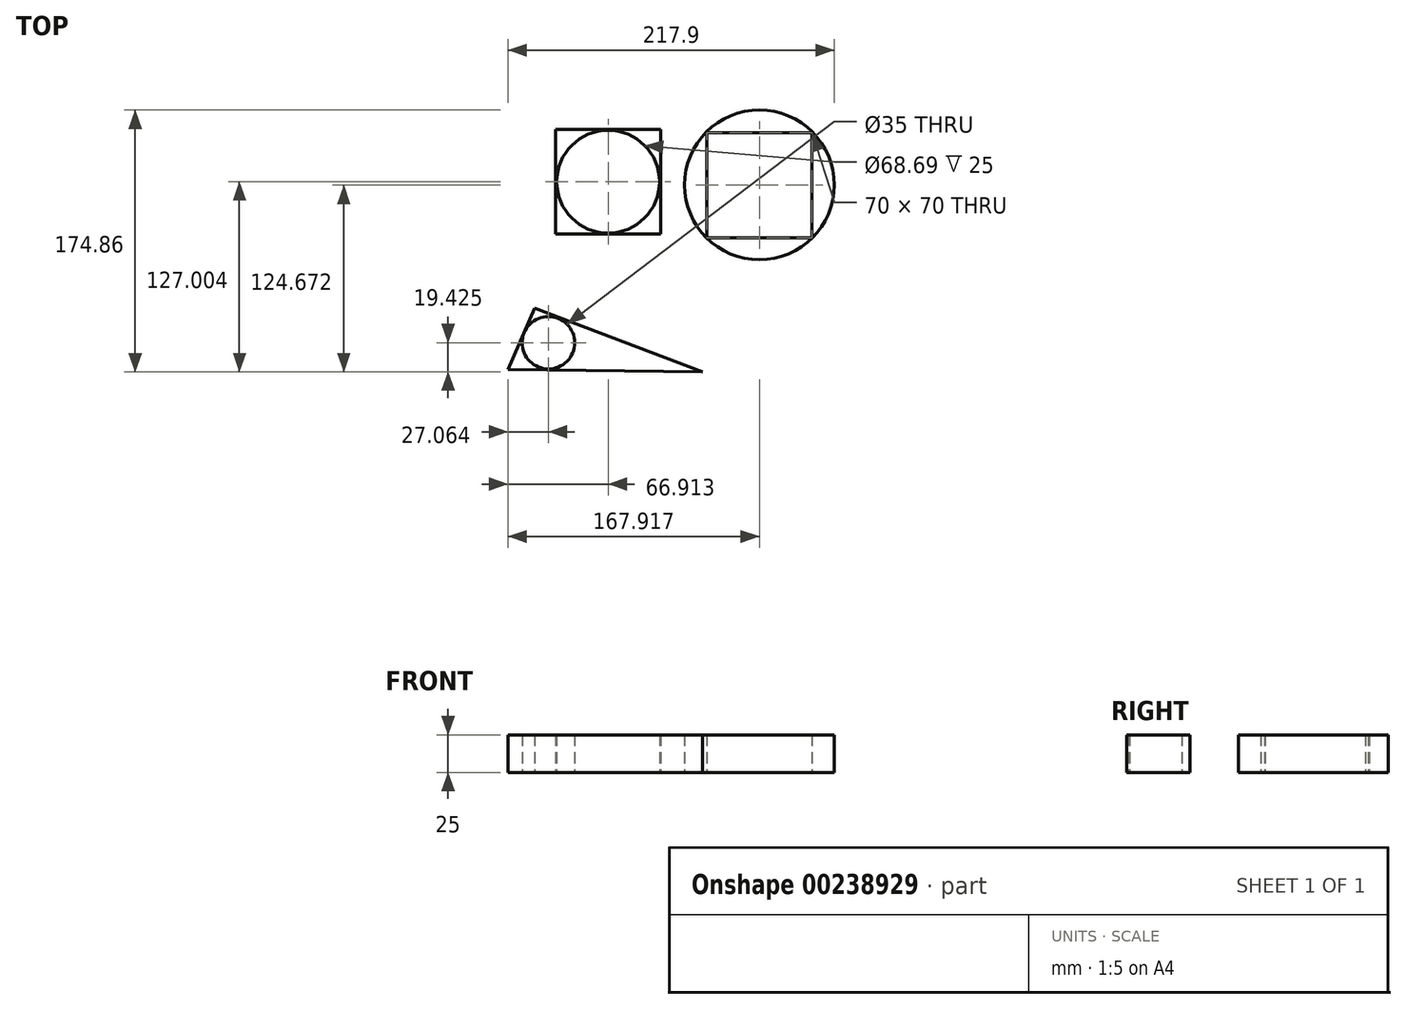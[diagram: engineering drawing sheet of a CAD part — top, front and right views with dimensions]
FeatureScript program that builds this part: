
annotation { "Feature Type Name" : "Feature", "Feature Type Description" : "" }
export const myFeature = defineFeature(function(context is Context, id is Id, definition is map)
    precondition{}
    {
        {
            var Q0;
            Q0=qCreatedBy(makeId("Top.planeOp"),FACE);
            var sketch = newSketch(context, id + "F0", { "sketchPlane" : qUnion([Q0])});
            skLineSegment(sketch, "E0", {"start": v(17.6, -74.14) * mm, "end": v(-94.65, -31.74) * mm});
            skLineSegment(sketch, "E1", {"start": v(17.6, -74.14) * mm, "end": v(-112.38, -72.57) * mm});
            skLineSegment(sketch, "E2", {"start": v(-94.65, -31.74) * mm, "end": v(-112.38, -72.57) * mm});
            skCircle(sketch, "E3", {"center": v(-85.32, -54.71) * mm, "radius": 17.5 * mm});
            skLineSegment(sketch, "E4", {"start": v(90.54, 85.53) * mm, "end": v(90.54, 15.53) * mm});
            skLineSegment(sketch, "E5", {"start": v(90.54, 15.53) * mm, "end": v(20.54, 15.53) * mm});
            skLineSegment(sketch, "E6", {"start": v(20.54, 15.53) * mm, "end": v(20.54, 85.53) * mm});
            skLineSegment(sketch, "E7", {"start": v(20.54, 85.53) * mm, "end": v(90.54, 85.53) * mm});
            skCircle(sketch, "E8", {"center": v(55.54, 50.74) * mm, "radius": 49.98 * mm});
            skLineSegment(sketch, "E9", {"start": v(-10.47, 87.95) * mm, "end": v(-10.47, 17.95) * mm});
            skLineSegment(sketch, "E10", {"start": v(-10.47, 87.95) * mm, "end": v(-80.47, 87.95) * mm});
            skLineSegment(sketch, "E11", {"start": v(-10.47, 17.95) * mm, "end": v(-80.47, 17.95) * mm});
            skLineSegment(sketch, "E12", {"start": v(-80.47, 87.95) * mm, "end": v(-80.47, 17.95) * mm});
            skCircle(sketch, "E13", {"center": v(-45.47, 52.86) * mm, "radius": 34.34 * mm});
            skSolve(sketch);
        }
        {
            var Q0;
            Q0 = qSketchRegion(id + "F0", true);
            extrude(context, id + "F1", {"entities" : qUnion([Q0]), "depth" : 25 * mm});
        }
    });
